# Revit family: Bidet_Frame-In_Wall-DXV-D29050044
name_source: partatom
category: Specialty Equipment
units: mm (PartAtom-declared; Revit-internal decimal feet)

## family parameters
Cut with Voids When Loaded = No
Host = Face
OmniClass Number = 23.45.05.21.14
OmniClass Title = Sanitary Disposal Components
Part Type = Normal
Room Calculation Point = No
Round Connector Dimension = Use Diameter
Shared = Yes

## types (1)
- D29050044.000
    Assembly Code = D2030400
    Compliance Certifications = Meets or Exceeds EPAct92 / ASME A112.6.2 / CSA B125.3
    Default Elevation = 0"
    Description = 2 in. X 6 in. In- wall bidet frame
    Finish = Steel-DXV-Powder Coated
    Floor Depth = 7 7/8"
    Floor Depth Constraint = 7 7/8"
    Height = 44 1/2"
    Inlet Connection Diameter = 1/2"
    Inlets Width = 11 7/16"
    Inlets Width Constraint = 11 7/16"
    Inlets Width/2 = 5 23/32"
    Installation Type = Recessed Wall Mounted
    Length = 5 3/16"
    Manufacturer = DXV
    Material = Steel-DXV-Powder Coated
    Model = D29050044.000
    Mounting Height = 12 5/8"
    Mounting Height Constraint = 12 5/8"
    Product Documentation Link = https://www.google.com
    Product Page URL = https://www.dxv.com
    URL = www.dxv.com
    Waste Connection Diameter = 2"
    Width = 19 7/16"

## geometry (parser evidence)
native form markers: Sweep x8
no freeform markers — native parametric forms only
